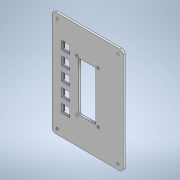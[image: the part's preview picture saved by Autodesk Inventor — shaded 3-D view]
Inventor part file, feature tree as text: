
AUTODESK INVENTOR PART (.ipt)
format: ipt  version: 2021 (Build 250183000, 183)  size: 259,072 bytes
history: native  units: mm
features: reference x32, sketch x8, extrude x7, other x3, pattern_linear x2
ambient origin geometry x8: Origin, YZ Plane, XZ Plane, XY Plane, X Axis, Y Axis, Z Axis, Center Point
bodies: Body1 (feature_tree)
feature tree (52):
  extrude  "Extrusion2"  Depth=3.0mm
  extrude  "Extrusion3"  Depth=2.0mm TaperAngle=0.0deg
  extrude  "Extrusion4"  Depth=2.0mm
  extrude  "Extrusion5"  Depth=0.2mm
  extrude  "Extrusion6"  Depth=0.2mm
  pattern_linear  "Rectangular Pattern1"  Count1=2  [1 undecoded]
  extrude  "Extrusion9"  Depth=2.0mm TaperAngle=0.0deg
  sketch  "Sketch10"  dims[d17=12.2mm]
  extrude  "Extrusion10"  Depth=20.0mm
  pattern_linear  "Rectangular Pattern3"  Count1=3  [1 undecoded]
  sketch  "Sketch2"  dims[d2=3.0mm d3=0.0mm d4=0.2mm]
  reference  "Reference9"
  reference  "Reference10"
  reference  "Reference11"
  reference  "Reference12"
  reference  "Reference13"
  reference  "Reference14"
  reference  "Reference15"
  reference  "Reference16"
  reference  "Reference17"
  reference  "Reference18"
  reference  "Reference19"
  reference  "Reference20"
  sketch  "Sketch3"  dims[d5=2.0mm d6=2.0mm d7=0.0mm]
  reference  "Reference21"
  reference  "Reference22"
  reference  "Reference23"
  reference  "Reference24"
  reference  "Reference25"
  reference  "Reference26"
  reference  "Reference27"
  reference  "Reference28"
  sketch  "Sketch4"  dims[d8=2.0mm d9=0.0mm d10=0.3mm]
  reference  "Reference29"
  reference  "Reference30"
  reference  "Reference31"
  reference  "Reference32"
  reference  "Reference33"
  reference  "Reference34"
  reference  "Reference35"
  reference  "Reference36"
  sketch  "Sketch5"  dims[d11=0.2mm d12=0.2mm]
  reference  "Reference37"
  reference  "Reference38"
  reference  "Reference39"
  reference  "Reference40"
  sketch  "Sketch6"  dims[d13=0.2mm d14=0.2mm]
  sketch  "Sketch9"  dims[d15=2.0mm d16=0.0mm]
  sketch  "Sketch11"  dims[d18=12.2mm d19=20.0mm d21=2.0mm d22=0.0mm d23=30.0mm d25=20.0mm d26=30.0mm d28=20.0mm d38=4.0mm d40=4.0mm d41=2.0mm d42=5.0mm d43=4.0mm d44=0.0mm d45=2.0mm d46=2.0mm d47=10.0mm d48=0.0mm d49=50.0mm d51=20.0mm]
  other  "Chestbox_with_electronical_devices.iam"
  other  "chestbox:1"
  other  "STEP 1602 Serial LCD Module:1"
note: 2 required parameter values undecoded (feature->parameter linkage not recoverable at this tier; creation-order binding heuristic only, values carry confidence <= 0.55)
